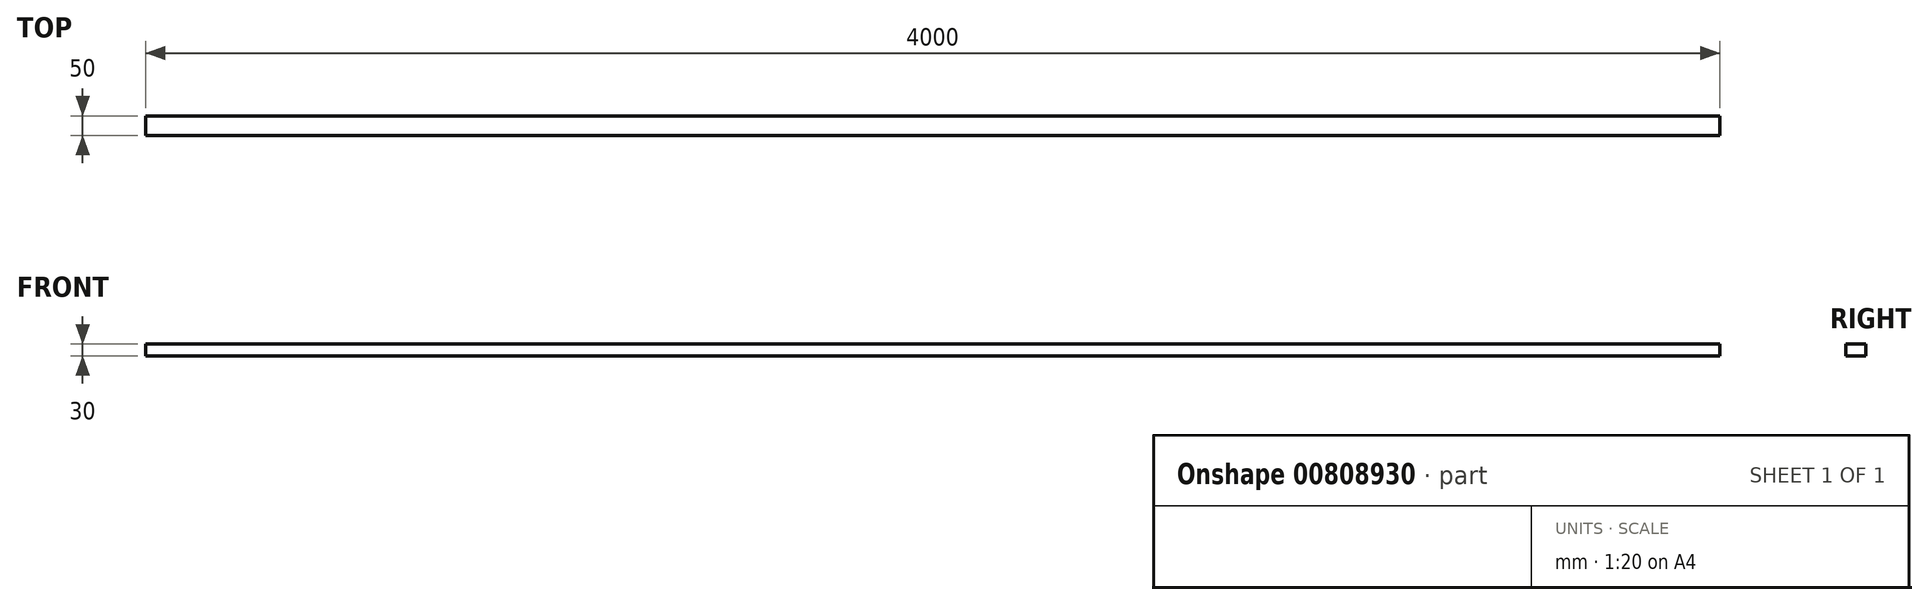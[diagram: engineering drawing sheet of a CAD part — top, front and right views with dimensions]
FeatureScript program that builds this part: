
annotation { "Feature Type Name" : "Feature", "Feature Type Description" : "" }
export const myFeature = defineFeature(function(context is Context, id is Id, definition is map)
    precondition{}
    {
        {
            var Q0;
            Q0=qCreatedBy(makeId("Right.planeOp"),FACE);
            var sketch = newSketch(context, id + "F0", { "sketchPlane" : qUnion([Q0])});
            skLineSegment(sketch, "E0.bottom", {"start": v(0, 0) * mm, "end": v(50, 0) * mm});
            skLineSegment(sketch, "E0.top", {"start": v(0, 30) * mm, "end": v(50, 30) * mm});
            skLineSegment(sketch, "E0.left", {"start": v(0, 0) * mm, "end": v(0, 30) * mm});
            skLineSegment(sketch, "E0.right", {"start": v(50, 0) * mm, "end": v(50, 30) * mm});
            skSolve(sketch);
        }
        {
            var Q0;
            Q0 = qSketchRegion(id + "F0", true);
            extrude(context, id + "F1", {"entities" : qUnion([Q0]), "oppositeDirection" : true, "depth" : 4000 * mm, "offsetDistance" : 25 * mm});
        }
    });
